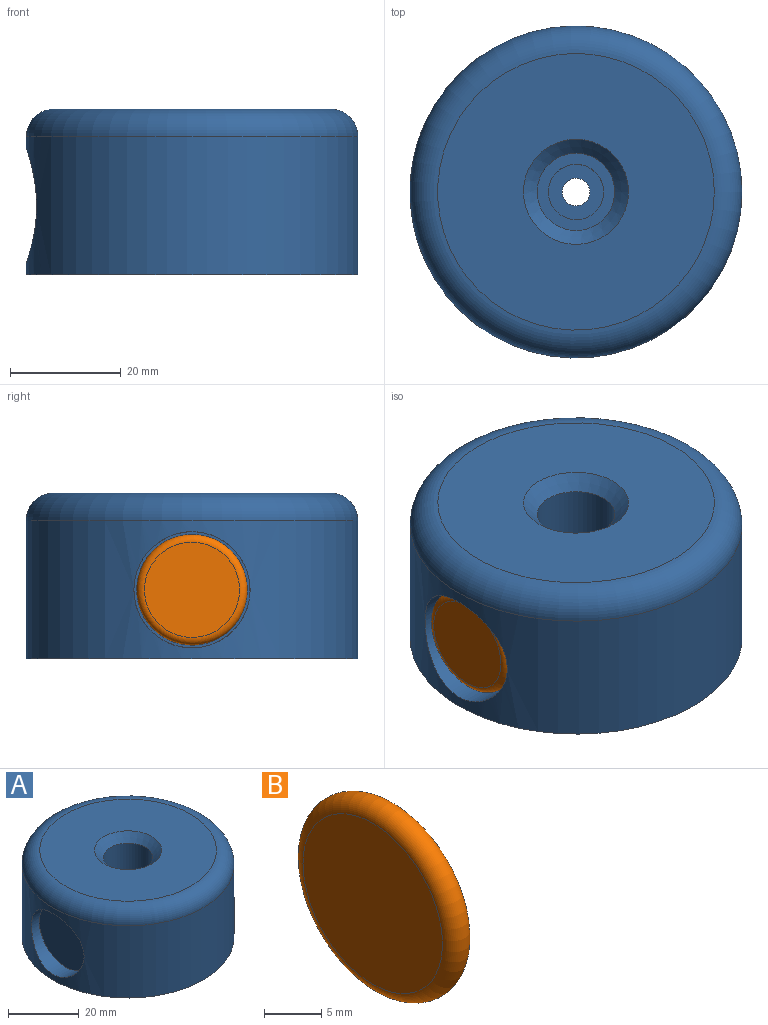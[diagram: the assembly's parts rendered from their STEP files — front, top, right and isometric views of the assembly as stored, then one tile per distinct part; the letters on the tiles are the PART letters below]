
ASSEMBLY  parts=2 mates=1
PART A: 12 faces, bbox 64.9x64.9x30 mm
  f0: cylinder r=30mm len=60mm, axis (0,0,-1), area 4360.8mm2, adj f2,f9,f10
  f1: plane 50x50mm, normal (0,0,1), area 1680mm2, adj f8,f9
  f2: plane 60x60mm, normal (0,0,-1), area 2807.8mm2, adj f0,f7
  f3: cylinder r=7mm len=15mm, axis (0,0,1), area 659.7mm2, adj f4,f8
  f4: plane 14x14mm, normal (0,0,1), area 75.4mm2, adj f3,f5
  f5: cylinder r=5mm len=10mm, axis (0,0,1), area 235.6mm2, adj f4,f6
  f6: plane 10x10mm, normal (0,0,1), area 58.9mm2, adj f5,f7
  f7: cylinder r=2.5mm len=5mm, axis (0,0,1), area 78.5mm2, adj f2,f6
  f8: cone r=7mm half-angle=45deg, axis (0,0,1), area 183.3mm2, adj f1,f3
  f9: torus R=25mm, axis (0,0,1), area 1390.8mm2, adj f0,f1
  f10: cylinder r=10.5mm len=21mm, axis (-1,0,0), area 267.9mm2, adj f0,f11
  f11: plane 21x21mm, normal (-1,0,0), area 346.4mm2, adj f10
PART B: 3 faces, bbox 2.8x21.6x21.6 mm
  f0: torus R=8.6mm, axis (-1,0,0), area 262.3mm2, adj f1,f2
  f1: plane 17.2x17.2mm, normal (1,0,0), area 232.4mm2, adj f0
  f2: plane 17.2x17.2mm, normal (-1,0,0), area 232.4mm2, adj f0
PLACE A t=(-25.74,-3.4,-5.7)mm
PLACE B t=(-53.54,-3.4,6.8)mm
MATE fastened A.f10 <-> B.f0  axis (-1,0,0) through (-50.74,-3.4,6.8)mm
